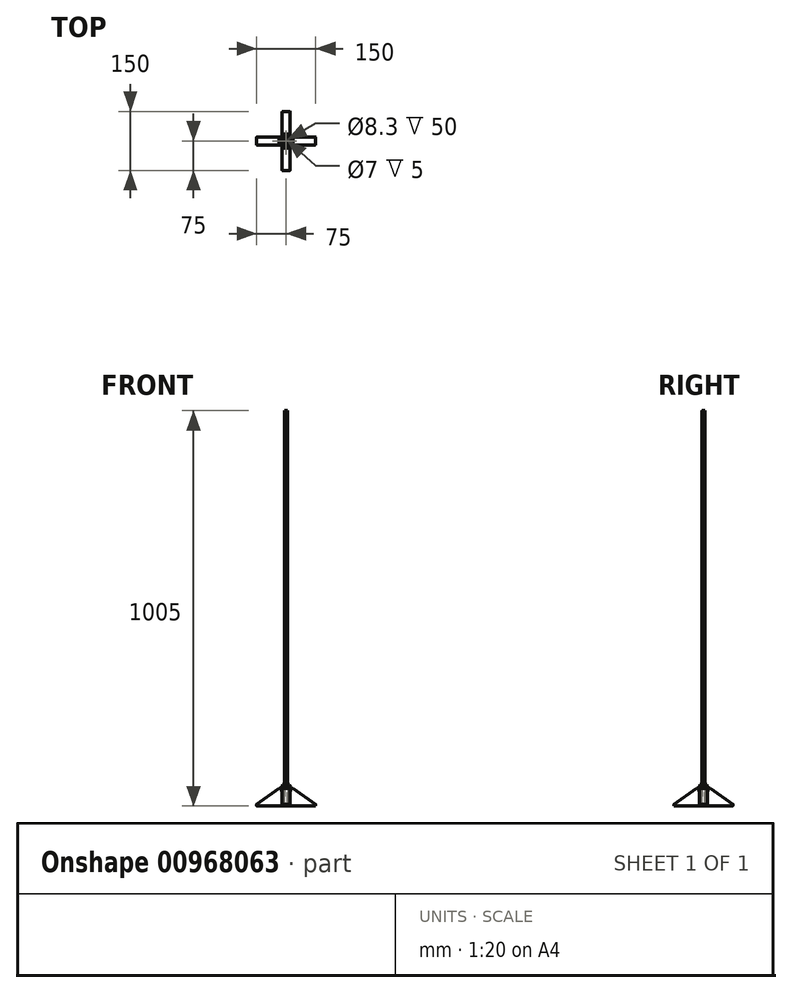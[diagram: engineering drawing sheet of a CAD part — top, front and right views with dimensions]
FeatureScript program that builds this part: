
annotation { "Feature Type Name" : "Feature", "Feature Type Description" : "" }
export const myFeature = defineFeature(function(context is Context, id is Id, definition is map)
    precondition{}
    {
        {
            var Q0;
            Q0=qCreatedBy(makeId("Top.planeOp"),FACE);
            var sketch = newSketch(context, id + "F0", { "sketchPlane" : qUnion([Q0])});
            skCircle(sketch, "E0", {"center": v(0, 0) * mm, "radius": 4.15 * mm});
            skCircle(sketch, "E1.0", {"center": v(0, 0) * mm, "radius": 9.15 * mm});
            skSolve(sketch);
        }
        {
            var Q0;
            Q0 = qSketchRegion(id + "F0", true);
            extrude(context, id + "F1", {"entities" : qUnion([Q0]), "depth" : 50 * mm, "offsetDistance" : 25 * mm});
        }
        {
            var Q0;
            Q0=makeQuery(id+"F1.opExtrude","CAP_FACE",FACE,{"disambiguationData":[OSD([sQuery(id+"F0.wireOp",EDGE,"E0"),sQuery(id+"F0.wireOp",EDGE,"E1.0")])],"isStart":true});
            var sketch = newSketch(context, id + "F2", { "sketchPlane" : qUnion([Q0])});
            skLineSegment(sketch, "E2.bottom", {"start": v(10, 75) * mm, "end": v(-10, 75) * mm});
            skLineSegment(sketch, "E2.top", {"start": v(10, -75) * mm, "end": v(-10, -75) * mm});
            skLineSegment(sketch, "E2.left", {"start": v(10, 75) * mm, "end": v(10, -75) * mm});
            skLineSegment(sketch, "E2.right", {"start": v(-10, 75) * mm, "end": v(-10, -75) * mm});
            skPoint(sketch, "E2.middle", {"position": v(0, 0) * mm});
            skLineSegment(sketch, "E3.bottom", {"start": v(75, 10) * mm, "end": v(-75, 10) * mm});
            skLineSegment(sketch, "E3.top", {"start": v(75, -10) * mm, "end": v(-75, -10) * mm});
            skLineSegment(sketch, "E3.left", {"start": v(75, 10) * mm, "end": v(75, -10) * mm});
            skLineSegment(sketch, "E3.right", {"start": v(-75, 10) * mm, "end": v(-75, -10) * mm});
            skSolve(sketch);
        }
        {
            var Q0;
            Q0 = qSketchRegion(id + "F2", true);
            extrude(context, id + "F3", {"entities" : qUnion([Q0]), "operationType" : NewBodyOperationType.ADD, "depth" : 5 * mm, "offsetDistance" : 25 * mm});
        }
        {
            var Q0;
            Q0=qCreatedBy(makeId("Right.planeOp"),FACE);
            var sketch = newSketch(context, id + "F4", { "sketchPlane" : qUnion([Q0])});
            skLineSegment(sketch, "E4", {"start": v(-75, 0) * mm, "end": v(0, 52.52) * mm});
            skLineSegment(sketch, "E5.MirrorCS", {"start": v(75, 0) * mm, "end": v(0, 52.52) * mm});
            skLineSegment(sketch, "E6", {"start": v(-75, 0) * mm, "end": v(-7, 0) * mm});
            skLineSegment(sketch, "E7", {"start": v(-7, 0) * mm, "end": v(-7, 47.61) * mm});
            skLineSegment(sketch, "E8.MirrorCS", {"start": v(7, 0) * mm, "end": v(7, 47.61) * mm});
            skLineSegment(sketch, "E9.MirrorCS", {"start": v(75, 0) * mm, "end": v(7, 0) * mm});
            skSolve(sketch);
        }
        {
            var Q0;
            {var subQ0=sQuery(id+"F4.wireOp",EDGE,"E6");Q0=makeQuery(id+"F4.imprint","IMPRINT",FACE,{"disambiguationData":[TD([[makeQuery(id+"F4.imprint","IMPRINT",EDGE,{"derivedFrom":subQ0}),1.0]])]});}
            var Q1;
            {var subQ2=sQuery(id+"F4.wireOp",EDGE,"E8.MirrorCS");Q1=makeQuery(id+"F4.imprint","IMPRINT",FACE,{"disambiguationData":[TD([[makeQuery(id+"F4.imprint","IMPRINT",EDGE,{"derivedFrom":subQ2}),-1.0]])]});}
            extrude(context, id + "F5", {"entities" : qUnion([Q0, Q1]), "operationType" : NewBodyOperationType.ADD, "endBound" : BoundingType.SYMMETRIC, "depth" : 20 * mm, "offsetDistance" : 25 * mm});
        }
        {
            var Q0;
            Q0=qCreatedBy(makeId("Front.planeOp"),FACE);
            var sketch = newSketch(context, id + "F6", { "sketchPlane" : qUnion([Q0])});
            skLineSegment(sketch, "E10", {"start": v(-75, 0) * mm, "end": v(0, 52.52) * mm});
            skLineSegment(sketch, "E11.MirrorCS", {"start": v(75, 0) * mm, "end": v(0, 52.52) * mm});
            skLineSegment(sketch, "E12", {"start": v(-75, 0) * mm, "end": v(-7, 0) * mm});
            skLineSegment(sketch, "E13", {"start": v(-7, 0) * mm, "end": v(-7, 47.61) * mm});
            skLineSegment(sketch, "E14.MirrorCS", {"start": v(7, 0) * mm, "end": v(7, 47.61) * mm});
            skLineSegment(sketch, "E15.MirrorCS", {"start": v(75, 0) * mm, "end": v(7, 0) * mm});
            skSolve(sketch);
        }
        {
            var Q0;
            Q0 = qSketchRegion(id + "F6", true);
            extrude(context, id + "F7", {"entities" : qUnion([Q0]), "operationType" : NewBodyOperationType.ADD, "endBound" : BoundingType.SYMMETRIC, "depth" : 20 * mm, "offsetDistance" : 25 * mm});
        }
        {
            var Q0;
            Q0=makeQuery(id+"F1.opExtrude","CAP_FACE",FACE,{"disambiguationData":[OSD([sQuery(id+"F0.wireOp",EDGE,"E0"),sQuery(id+"F0.wireOp",EDGE,"E1.0")])],"isStart":false});
            var sketch = newSketch(context, id + "F8", { "sketchPlane" : qUnion([Q0])});
            skCircle(sketch, "E16", {"center": v(0, 0) * mm, "radius": 9 * mm});
            skCircle(sketch, "E17", {"center": v(0, 0) * mm, "radius": 20 * mm});
            skSolve(sketch);
        }
        {
            var Q0;
            Q0 = qSketchRegion(id + "F8", true);
            extrude(context, id + "F9", {"entities" : qUnion([Q0]), "operationType" : NewBodyOperationType.REMOVE, "oppositeDirection" : true, "depth" : 10 * mm, "offsetDistance" : 25 * mm});
        }
        {
            var Q0;
            Q0=makeQuery(id+"F9.boolean.opBoolean","COPY",FACE,{"derivedFrom":makeQuery(id+"F9.opExtrude","CAP_FACE",FACE,{"disambiguationData":[OSD([sQuery(id+"F8.wireOp",EDGE,"E16"),sQuery(id+"F8.wireOp",EDGE,"E17")])],"isStart":false})});
            var sketch = newSketch(context, id + "F10", { "sketchPlane" : qUnion([Q0])});
            skCircle(sketch, "E18", {"center": v(0, 0) * mm, "radius": 12.5 * mm});
            skSolve(sketch);
        }
        {
            var Q0;
            {var subQ0=makeQuery(id+"F9.opExtrude","CAP_FACE",FACE,{"disambiguationData":[OSD([sQuery(id+"F8.wireOp",EDGE,"E16"),sQuery(id+"F8.wireOp",EDGE,"E17")])],"isStart":false});var subQ9=makeQuery(id+"F1.opExtrude","SWEPT_FACE",FACE,{"disambiguationData":[OSD([sQuery(id+"F0.wireOp",EDGE,"E1.0")])]});Q0=makeQuery(id+"F10.imprint","IMPRINT",FACE,{"disambiguationData":[TD([[makeQuery(id+"F10.imprint","IMPRINT",EDGE,{"derivedFrom":makeQuery(id+"F9.boolean.opBoolean","INTERSECT",EDGE,{"disambiguationData":[OD(0.0)],"derivedFrom":[subQ9,subQ0]})}),-1.0]])]});}
            var Q1;
            {var subQ0=makeQuery(id+"F9.opExtrude","CAP_FACE",FACE,{"disambiguationData":[OSD([sQuery(id+"F8.wireOp",EDGE,"E16"),sQuery(id+"F8.wireOp",EDGE,"E17")])],"isStart":false});var subQ9=makeQuery(id+"F1.opExtrude","SWEPT_FACE",FACE,{"disambiguationData":[OSD([sQuery(id+"F0.wireOp",EDGE,"E1.0")])]});Q1=makeQuery(id+"F10.imprint","IMPRINT",FACE,{"disambiguationData":[TD([[makeQuery(id+"F10.imprint","IMPRINT",EDGE,{"derivedFrom":makeQuery(id+"F9.boolean.opBoolean","INTERSECT",EDGE,{"disambiguationData":[OD(1.0)],"derivedFrom":[subQ9,subQ0]})}),-1.0]])]});}
            var Q2;
            {var subQ0=makeQuery(id+"F9.opExtrude","CAP_FACE",FACE,{"disambiguationData":[OSD([sQuery(id+"F8.wireOp",EDGE,"E16"),sQuery(id+"F8.wireOp",EDGE,"E17")])],"isStart":false});var subQ3=makeQuery(id+"F1.opExtrude","SWEPT_FACE",FACE,{"disambiguationData":[OSD([sQuery(id+"F0.wireOp",EDGE,"E1.0")])]});Q2=makeQuery(id+"F10.imprint","IMPRINT",FACE,{"disambiguationData":[TD([[makeQuery(id+"F10.imprint","IMPRINT",EDGE,{"derivedFrom":makeQuery(id+"F9.boolean.opBoolean","INTERSECT",EDGE,{"disambiguationData":[OD(2.0)],"derivedFrom":[subQ3,subQ0]})}),-1.0]])]});}
            var Q3;
            {var subQ0=makeQuery(id+"F9.opExtrude","CAP_FACE",FACE,{"disambiguationData":[OSD([sQuery(id+"F8.wireOp",EDGE,"E16"),sQuery(id+"F8.wireOp",EDGE,"E17")])],"isStart":false});var subQ3=makeQuery(id+"F1.opExtrude","SWEPT_FACE",FACE,{"disambiguationData":[OSD([sQuery(id+"F0.wireOp",EDGE,"E1.0")])]});Q3=makeQuery(id+"F10.imprint","IMPRINT",FACE,{"disambiguationData":[TD([[makeQuery(id+"F10.imprint","IMPRINT",EDGE,{"derivedFrom":makeQuery(id+"F9.boolean.opBoolean","INTERSECT",EDGE,{"disambiguationData":[OD(3.0)],"derivedFrom":[subQ3,subQ0]})}),-1.0]])]});}
            var Q4;
            Q4=makeQuery(id+"F10.imprint","IMPRINT",FACE,{"disambiguationData":[TD([[makeQuery(id+"F10.imprint","IMPRINT",EDGE,{"derivedFrom":sQuery(id+"F10.wireOp",EDGE,"E18")}),1.0]])]});
            extrude(context, id + "F11", {"entities" : qUnion([Q0, Q1, Q2, Q3, Q4]), "operationType" : NewBodyOperationType.ADD, "depth" : 5 * mm, "offsetDistance" : 25 * mm});
        }
        {
            var Q0;
            {var subQ2=sQuery(id+"F2.wireOp",EDGE,"E2.left");var subQ5=sQuery(id+"F2.wireOp",EDGE,"E2.bottom");var subQ6=makeQuery(id+"F3.opExtrude","SWEPT_FACE",FACE,{"disambiguationData":[OSD([subQ2]),TDD([makeQuery(id+"F2.imprint","IMPRINT",EDGE,{"disambiguationData":[TD([[makeQuery(id+"F2.imprint","INTERSECT",VERTEX,{"derivedFrom":[subQ5,subQ2]}),-1.0]])],"derivedFrom":subQ2})])]});var subQ7=sQuery(id+"F4.wireOp",EDGE,"E4");var subQ8=makeQuery(id+"F5.opExtrude","CAP_FACE",FACE,{"disambiguationData":[OSD([subQ7,sQuery(id+"F4.wireOp",EDGE,"E6"),sQuery(id+"F4.wireOp",EDGE,"E7")])],"isStart":false});Q0=makeQuery(id+"F7.boolean.opBoolean","SPLIT",FACE,{"disambiguationData":[TD([makeQuery(id+"F3.opExtrude","SWEPT_FACE",FACE,{"disambiguationData":[OSD([subQ5])]})])],"derivedFrom":makeQuery(id+"F5.boolean.opBoolean","MERGE",FACE,{"derivedFrom":[subQ6,subQ8]})});}
            var sketch = newSketch(context, id + "F12", { "sketchPlane" : qUnion([Q0])});
            skLineSegment(sketch, "E19.bottom", {"start": v(-13.66, 40) * mm, "end": v(-49.71, 40) * mm});
            skLineSegment(sketch, "E19.top", {"start": v(-13.66, 51.4) * mm, "end": v(-49.71, 51.4) * mm});
            skLineSegment(sketch, "E19.left", {"start": v(-13.66, 40) * mm, "end": v(-13.66, 51.4) * mm});
            skLineSegment(sketch, "E19.right", {"start": v(-49.71, 40) * mm, "end": v(-49.71, 51.4) * mm});
            skSolve(sketch);
        }
        {
            var Q0;
            Q0 = qSketchRegion(id + "F12", true);
            extrude(context, id + "F13", {"entities" : qUnion([Q0]), "operationType" : NewBodyOperationType.REMOVE, "oppositeDirection" : true, "depth" : 51.9 * mm, "offsetDistance" : 25 * mm});
        }
        {
            var Q0;
            {var subQ0=sQuery(id+"F2.wireOp",EDGE,"E3.bottom");Q0=makeQuery(id+"F7.boolean.opBoolean","MERGE",FACE,{"derivedFrom":[makeQuery(id+"F3.opExtrude","SWEPT_FACE",FACE,{"disambiguationData":[OSD([subQ0]),TDD([makeQuery(id+"F2.imprint","IMPRINT",EDGE,{"disambiguationData":[TD([[makeQuery(id+"F2.imprint","INTERSECT",VERTEX,{"derivedFrom":[subQ0,sQuery(id+"F2.wireOp",EDGE,"E3.right")]}),1.0]])],"derivedFrom":subQ0})])]}),makeQuery(id+"F7.opExtrude","CAP_FACE",FACE,{"disambiguationData":[OSD([sQuery(id+"F6.wireOp",EDGE,"E10"),sQuery(id+"F6.wireOp",EDGE,"E12"),sQuery(id+"F6.wireOp",EDGE,"E13")])],"isStart":false})]});}
            var sketch = newSketch(context, id + "F14", { "sketchPlane" : qUnion([Q0])});
            skLineSegment(sketch, "E20.bottom", {"start": v(-13.66, 40) * mm, "end": v(-64.64, 40) * mm});
            skLineSegment(sketch, "E20.top", {"start": v(-13.66, 50.99) * mm, "end": v(-64.64, 50.99) * mm});
            skLineSegment(sketch, "E20.left", {"start": v(-13.66, 40) * mm, "end": v(-13.66, 50.99) * mm});
            skLineSegment(sketch, "E20.right", {"start": v(-64.64, 40) * mm, "end": v(-64.64, 50.99) * mm});
            skSolve(sketch);
        }
        {
            var Q0;
            Q0 = qSketchRegion(id + "F14", true);
            extrude(context, id + "F15", {"entities" : qUnion([Q0]), "operationType" : NewBodyOperationType.REMOVE, "oppositeDirection" : true, "depth" : 25 * mm, "offsetDistance" : 25 * mm});
        }
        {
            var Q0;
            {var subQ2=sQuery(id+"F2.wireOp",EDGE,"E2.right");var subQ4=sQuery(id+"F2.wireOp",EDGE,"E2.top");var subQ6=makeQuery(id+"F3.opExtrude","SWEPT_FACE",FACE,{"disambiguationData":[OSD([subQ2]),TDD([makeQuery(id+"F2.imprint","IMPRINT",EDGE,{"disambiguationData":[TD([[makeQuery(id+"F2.imprint","INTERSECT",VERTEX,{"derivedFrom":[subQ4,subQ2]}),1.0]])],"derivedFrom":subQ2})])]});var subQ7=sQuery(id+"F4.wireOp",EDGE,"E5.MirrorCS");var subQ8=makeQuery(id+"F5.opExtrude","CAP_FACE",FACE,{"disambiguationData":[OSD([subQ7,sQuery(id+"F4.wireOp",EDGE,"E8.MirrorCS"),sQuery(id+"F4.wireOp",EDGE,"E9.MirrorCS")])],"isStart":true});Q0=makeQuery(id+"F7.boolean.opBoolean","SPLIT",FACE,{"disambiguationData":[TD([makeQuery(id+"F3.opExtrude","SWEPT_FACE",FACE,{"disambiguationData":[OSD([subQ4])]})])],"derivedFrom":makeQuery(id+"F5.boolean.opBoolean","MERGE",FACE,{"derivedFrom":[subQ6,subQ8]})});}
            var sketch = newSketch(context, id + "F16", { "sketchPlane" : qUnion([Q0])});
            skLineSegment(sketch, "E21.bottom", {"start": v(-15.31, 40) * mm, "end": v(-53.85, 40) * mm});
            skLineSegment(sketch, "E21.top", {"start": v(-15.31, 53.3) * mm, "end": v(-53.85, 53.3) * mm});
            skLineSegment(sketch, "E21.left", {"start": v(-15.31, 40) * mm, "end": v(-15.31, 53.3) * mm});
            skLineSegment(sketch, "E21.right", {"start": v(-53.85, 40) * mm, "end": v(-53.85, 53.3) * mm});
            skSolve(sketch);
        }
        {
            var Q0;
            Q0 = qSketchRegion(id + "F16", true);
            extrude(context, id + "F17", {"entities" : qUnion([Q0]), "operationType" : NewBodyOperationType.REMOVE, "oppositeDirection" : true, "depth" : 25 * mm, "offsetDistance" : 25 * mm});
        }
        {
            var Q0;
            {var subQ0=sQuery(id+"F2.wireOp",EDGE,"E3.top");Q0=makeQuery(id+"F7.boolean.opBoolean","MERGE",FACE,{"derivedFrom":[makeQuery(id+"F3.opExtrude","SWEPT_FACE",FACE,{"disambiguationData":[OSD([subQ0]),TDD([makeQuery(id+"F2.imprint","IMPRINT",EDGE,{"disambiguationData":[TD([[makeQuery(id+"F2.imprint","INTERSECT",VERTEX,{"derivedFrom":[subQ0,sQuery(id+"F2.wireOp",EDGE,"E3.left")]}),-1.0]])],"derivedFrom":subQ0})])]}),makeQuery(id+"F7.opExtrude","CAP_FACE",FACE,{"disambiguationData":[OSD([sQuery(id+"F6.wireOp",EDGE,"E11.MirrorCS"),sQuery(id+"F6.wireOp",EDGE,"E14.MirrorCS"),sQuery(id+"F6.wireOp",EDGE,"E15.MirrorCS")])],"isStart":true})]});}
            var sketch = newSketch(context, id + "F18", { "sketchPlane" : qUnion([Q0])});
            skLineSegment(sketch, "E22.bottom", {"start": v(-13.66, 40) * mm, "end": v(-70.3, 40) * mm});
            skLineSegment(sketch, "E22.top", {"start": v(-13.66, 49.17) * mm, "end": v(-70.3, 49.17) * mm});
            skLineSegment(sketch, "E22.left", {"start": v(-13.66, 40) * mm, "end": v(-13.66, 49.17) * mm});
            skLineSegment(sketch, "E22.right", {"start": v(-70.3, 40) * mm, "end": v(-70.3, 49.17) * mm});
            skSolve(sketch);
        }
        {
            var Q0;
            Q0 = qSketchRegion(id + "F18", true);
            extrude(context, id + "F19", {"entities" : qUnion([Q0]), "operationType" : NewBodyOperationType.REMOVE, "oppositeDirection" : true, "depth" : 25 * mm, "offsetDistance" : 25 * mm});
        }
        {
            var Q0;
            Q0=makeQuery(id+"F11.opExtrude","CAP_EDGE",EDGE,{"disambiguationData":[OSD([sQuery(id+"F10.wireOp",EDGE,"E18")])],"isStart":false});
            var Q1;
            Q1=makeQuery(id+"F9.boolean.opBoolean","COPY",EDGE,{"derivedFrom":makeQuery(id+"F9.opExtrude","CAP_EDGE",EDGE,{"disambiguationData":[OSD([sQuery(id+"F8.wireOp",EDGE,"E16")])],"isStart":true})});
            fillet(context, id + "F20", {"entities" : qUnion([Q0, Q1]), "radius" : 2 * mm, "tangentPropagation" : true, "allowEdgeOverflow" : false});
        }
        {
            var Q0;
            Q0=makeQuery(id+"F3.boolean.opBoolean","SPLIT",FACE,{"disambiguationData":[TD([makeQuery(id+"F1.opExtrude","SWEPT_FACE",FACE,{"disambiguationData":[OSD([sQuery(id+"F0.wireOp",EDGE,"E0")])]})])],"derivedFrom":makeQuery(id+"F3.opExtrude","CAP_FACE",FACE,{"disambiguationData":[OSD([sQuery(id+"F2.wireOp",EDGE,"E2.bottom"),sQuery(id+"F2.wireOp",EDGE,"E2.top"),sQuery(id+"F2.wireOp",EDGE,"E2.left"),sQuery(id+"F2.wireOp",EDGE,"E2.right"),sQuery(id+"F2.wireOp",EDGE,"E3.bottom"),sQuery(id+"F2.wireOp",EDGE,"E3.top"),sQuery(id+"F2.wireOp",EDGE,"E3.left"),sQuery(id+"F2.wireOp",EDGE,"E3.right")])],"isStart":true})});
            var sketch = newSketch(context, id + "F21", { "sketchPlane" : qUnion([Q0])});
            skCircle(sketch, "E23", {"center": v(0, 0) * mm, "radius": 3.5 * mm});
            skSolve(sketch);
        }
        {
            var Q0;
            Q0 = qSketchRegion(id + "F21", true);
            extrude(context, id + "F22", {"entities" : qUnion([Q0]), "operationType" : NewBodyOperationType.REMOVE, "oppositeDirection" : true, "depth" : 25 * mm, "offsetDistance" : 25 * mm});
        }
        {
            var Q0;
            {var subQ0=sQuery(id+"F2.wireOp",EDGE,"E3.bottom");var subQ1=sQuery(id+"F6.wireOp",EDGE,"E10");Q0=makeQuery(id+"F7.boolean.opBoolean","SPLIT",EDGE,{"disambiguationData":[topologyDisambiguationEdgeConnected([makeQuery(id+"F3.opExtrude","SWEPT_FACE",FACE,{"disambiguationData":[OSD([subQ0]),TDD([makeQuery(id+"F2.imprint","IMPRINT",EDGE,{"disambiguationData":[TD([[makeQuery(id+"F2.imprint","INTERSECT",VERTEX,{"derivedFrom":[subQ0,sQuery(id+"F2.wireOp",EDGE,"E3.right")]}),1.0]])],"derivedFrom":subQ0})])]}),makeQuery(id+"F7.opExtrude","SWEPT_FACE",FACE,{"disambiguationData":[OSD([subQ1])]}),makeQuery(id+"F7.opExtrude","CAP_FACE",FACE,{"disambiguationData":[OSD([subQ1,sQuery(id+"F6.wireOp",EDGE,"E12"),sQuery(id+"F6.wireOp",EDGE,"E13")])],"isStart":false})])],"derivedFrom":makeQuery(id+"F7.opExtrude","CAP_EDGE",EDGE,{"disambiguationData":[OSD([subQ1])],"isStart":false})});}
            var Q1;
            {var subQ3=sQuery(id+"F4.wireOp",EDGE,"E5.MirrorCS");var subQ4=sQuery(id+"F2.wireOp",EDGE,"E2.top");Q1=makeQuery(id+"F7.boolean.opBoolean","SPLIT",EDGE,{"disambiguationData":[TD([makeQuery(id+"F3.opExtrude","SWEPT_FACE",FACE,{"disambiguationData":[OSD([subQ4])]})])],"derivedFrom":makeQuery(id+"F5.opExtrude","CAP_EDGE",EDGE,{"disambiguationData":[OSD([subQ3])],"isStart":true})});}
            var Q2;
            {var subQ0=sQuery(id+"F2.wireOp",EDGE,"E3.top");var subQ1=sQuery(id+"F6.wireOp",EDGE,"E10");Q2=makeQuery(id+"F7.boolean.opBoolean","SPLIT",EDGE,{"disambiguationData":[topologyDisambiguationEdgeConnected([makeQuery(id+"F3.opExtrude","SWEPT_FACE",FACE,{"disambiguationData":[OSD([subQ0]),TDD([makeQuery(id+"F2.imprint","IMPRINT",EDGE,{"disambiguationData":[TD([[makeQuery(id+"F2.imprint","INTERSECT",VERTEX,{"derivedFrom":[subQ0,sQuery(id+"F2.wireOp",EDGE,"E3.right")]}),1.0]])],"derivedFrom":subQ0})])]}),makeQuery(id+"F7.opExtrude","SWEPT_FACE",FACE,{"disambiguationData":[OSD([subQ1])]}),makeQuery(id+"F7.opExtrude","CAP_FACE",FACE,{"disambiguationData":[OSD([subQ1,sQuery(id+"F6.wireOp",EDGE,"E12"),sQuery(id+"F6.wireOp",EDGE,"E13")])],"isStart":true})])],"derivedFrom":makeQuery(id+"F7.opExtrude","CAP_EDGE",EDGE,{"disambiguationData":[OSD([subQ1])],"isStart":true})});}
            var Q3;
            {var subQ0=sQuery(id+"F4.wireOp",EDGE,"E5.MirrorCS");var subQ4=sQuery(id+"F2.wireOp",EDGE,"E2.top");Q3=makeQuery(id+"F7.boolean.opBoolean","SPLIT",EDGE,{"disambiguationData":[TD([makeQuery(id+"F3.opExtrude","SWEPT_FACE",FACE,{"disambiguationData":[OSD([subQ4])]})])],"derivedFrom":makeQuery(id+"F5.opExtrude","CAP_EDGE",EDGE,{"disambiguationData":[OSD([subQ0])],"isStart":false})});}
            var Q4;
            {var subQ0=sQuery(id+"F2.wireOp",EDGE,"E3.top");var subQ1=sQuery(id+"F6.wireOp",EDGE,"E11.MirrorCS");Q4=makeQuery(id+"F7.boolean.opBoolean","SPLIT",EDGE,{"disambiguationData":[topologyDisambiguationEdgeConnected([makeQuery(id+"F3.opExtrude","SWEPT_FACE",FACE,{"disambiguationData":[OSD([subQ0]),TDD([makeQuery(id+"F2.imprint","IMPRINT",EDGE,{"disambiguationData":[TD([[makeQuery(id+"F2.imprint","INTERSECT",VERTEX,{"derivedFrom":[subQ0,sQuery(id+"F2.wireOp",EDGE,"E3.left")]}),-1.0]])],"derivedFrom":subQ0})])]}),makeQuery(id+"F7.opExtrude","SWEPT_FACE",FACE,{"disambiguationData":[OSD([subQ1])]}),makeQuery(id+"F7.opExtrude","CAP_FACE",FACE,{"disambiguationData":[OSD([subQ1,sQuery(id+"F6.wireOp",EDGE,"E14.MirrorCS"),sQuery(id+"F6.wireOp",EDGE,"E15.MirrorCS")])],"isStart":true})])],"derivedFrom":makeQuery(id+"F7.opExtrude","CAP_EDGE",EDGE,{"disambiguationData":[OSD([subQ1])],"isStart":true})});}
            var Q5;
            {var subQ0=sQuery(id+"F2.wireOp",EDGE,"E3.bottom");var subQ1=sQuery(id+"F6.wireOp",EDGE,"E11.MirrorCS");Q5=makeQuery(id+"F7.boolean.opBoolean","SPLIT",EDGE,{"disambiguationData":[topologyDisambiguationEdgeConnected([makeQuery(id+"F3.opExtrude","SWEPT_FACE",FACE,{"disambiguationData":[OSD([subQ0]),TDD([makeQuery(id+"F2.imprint","IMPRINT",EDGE,{"disambiguationData":[TD([[makeQuery(id+"F2.imprint","INTERSECT",VERTEX,{"derivedFrom":[subQ0,sQuery(id+"F2.wireOp",EDGE,"E3.left")]}),-1.0]])],"derivedFrom":subQ0})])]}),makeQuery(id+"F7.opExtrude","SWEPT_FACE",FACE,{"disambiguationData":[OSD([subQ1])]}),makeQuery(id+"F7.opExtrude","CAP_FACE",FACE,{"disambiguationData":[OSD([subQ1,sQuery(id+"F6.wireOp",EDGE,"E14.MirrorCS"),sQuery(id+"F6.wireOp",EDGE,"E15.MirrorCS")])],"isStart":false})])],"derivedFrom":makeQuery(id+"F7.opExtrude","CAP_EDGE",EDGE,{"disambiguationData":[OSD([subQ1])],"isStart":false})});}
            var Q6;
            {var subQ4=sQuery(id+"F4.wireOp",EDGE,"E4");var subQ5=sQuery(id+"F2.wireOp",EDGE,"E2.bottom");Q6=makeQuery(id+"F7.boolean.opBoolean","SPLIT",EDGE,{"disambiguationData":[TD([makeQuery(id+"F3.opExtrude","SWEPT_FACE",FACE,{"disambiguationData":[OSD([subQ5])]})])],"derivedFrom":makeQuery(id+"F5.opExtrude","CAP_EDGE",EDGE,{"disambiguationData":[OSD([subQ4])],"isStart":false})});}
            var Q7;
            {var subQ0=sQuery(id+"F4.wireOp",EDGE,"E4");var subQ5=sQuery(id+"F2.wireOp",EDGE,"E2.bottom");Q7=makeQuery(id+"F7.boolean.opBoolean","SPLIT",EDGE,{"disambiguationData":[TD([makeQuery(id+"F3.opExtrude","SWEPT_FACE",FACE,{"disambiguationData":[OSD([subQ5])]})])],"derivedFrom":makeQuery(id+"F5.opExtrude","CAP_EDGE",EDGE,{"disambiguationData":[OSD([subQ0])],"isStart":true})});}
            fillet(context, id + "F23", {"entities" : qUnion([Q0, Q1, Q2, Q3, Q4, Q5, Q6, Q7]), "radius" : 5 * mm, "tangentPropagation" : true, "allowEdgeOverflow" : false});
        }
        {
            var Q0;
            {var subQ0=sQuery(id+"F2.wireOp",EDGE,"E2.right");Q0=makeQuery(id+"F7.boolean.opBoolean","INTERSECT",EDGE,{"derivedFrom":[makeQuery(id+"F5.boolean.opBoolean","MERGE",FACE,{"derivedFrom":[makeQuery(id+"F3.opExtrude","SWEPT_FACE",FACE,{"disambiguationData":[OSD([subQ0]),TDD([makeQuery(id+"F2.imprint","IMPRINT",EDGE,{"disambiguationData":[TD([[makeQuery(id+"F2.imprint","INTERSECT",VERTEX,{"derivedFrom":[sQuery(id+"F2.wireOp",EDGE,"E2.bottom"),subQ0]}),-1.0]])],"derivedFrom":subQ0})])]}),makeQuery(id+"F5.opExtrude","CAP_FACE",FACE,{"disambiguationData":[OSD([sQuery(id+"F4.wireOp",EDGE,"E4"),sQuery(id+"F4.wireOp",EDGE,"E6"),sQuery(id+"F4.wireOp",EDGE,"E7")])],"isStart":true})]}),makeQuery(id+"F7.opExtrude","CAP_FACE",FACE,{"disambiguationData":[OSD([sQuery(id+"F6.wireOp",EDGE,"E10"),sQuery(id+"F6.wireOp",EDGE,"E12"),sQuery(id+"F6.wireOp",EDGE,"E13")])],"isStart":false})]});}
            var Q1;
            {var subQ0=sQuery(id+"F2.wireOp",EDGE,"E2.left");Q1=makeQuery(id+"F7.boolean.opBoolean","INTERSECT",EDGE,{"derivedFrom":[makeQuery(id+"F5.boolean.opBoolean","MERGE",FACE,{"derivedFrom":[makeQuery(id+"F3.opExtrude","SWEPT_FACE",FACE,{"disambiguationData":[OSD([subQ0]),TDD([makeQuery(id+"F2.imprint","IMPRINT",EDGE,{"disambiguationData":[TD([[makeQuery(id+"F2.imprint","INTERSECT",VERTEX,{"derivedFrom":[sQuery(id+"F2.wireOp",EDGE,"E2.bottom"),subQ0]}),-1.0]])],"derivedFrom":subQ0})])]}),makeQuery(id+"F5.opExtrude","CAP_FACE",FACE,{"disambiguationData":[OSD([sQuery(id+"F4.wireOp",EDGE,"E4"),sQuery(id+"F4.wireOp",EDGE,"E6"),sQuery(id+"F4.wireOp",EDGE,"E7")])],"isStart":false})]}),makeQuery(id+"F7.opExtrude","CAP_FACE",FACE,{"disambiguationData":[OSD([sQuery(id+"F6.wireOp",EDGE,"E11.MirrorCS"),sQuery(id+"F6.wireOp",EDGE,"E14.MirrorCS"),sQuery(id+"F6.wireOp",EDGE,"E15.MirrorCS")])],"isStart":false})]});}
            var Q2;
            {var subQ0=sQuery(id+"F2.wireOp",EDGE,"E2.left");Q2=makeQuery(id+"F7.boolean.opBoolean","INTERSECT",EDGE,{"derivedFrom":[makeQuery(id+"F5.boolean.opBoolean","MERGE",FACE,{"derivedFrom":[makeQuery(id+"F3.opExtrude","SWEPT_FACE",FACE,{"disambiguationData":[OSD([subQ0]),TDD([makeQuery(id+"F2.imprint","IMPRINT",EDGE,{"disambiguationData":[TD([[makeQuery(id+"F2.imprint","INTERSECT",VERTEX,{"derivedFrom":[sQuery(id+"F2.wireOp",EDGE,"E2.top"),subQ0]}),1.0]])],"derivedFrom":subQ0})])]}),makeQuery(id+"F5.opExtrude","CAP_FACE",FACE,{"disambiguationData":[OSD([sQuery(id+"F4.wireOp",EDGE,"E5.MirrorCS"),sQuery(id+"F4.wireOp",EDGE,"E8.MirrorCS"),sQuery(id+"F4.wireOp",EDGE,"E9.MirrorCS")])],"isStart":false})]}),makeQuery(id+"F7.opExtrude","CAP_FACE",FACE,{"disambiguationData":[OSD([sQuery(id+"F6.wireOp",EDGE,"E11.MirrorCS"),sQuery(id+"F6.wireOp",EDGE,"E14.MirrorCS"),sQuery(id+"F6.wireOp",EDGE,"E15.MirrorCS")])],"isStart":true})]});}
            var Q3;
            {var subQ0=sQuery(id+"F2.wireOp",EDGE,"E2.right");Q3=makeQuery(id+"F7.boolean.opBoolean","INTERSECT",EDGE,{"derivedFrom":[makeQuery(id+"F5.boolean.opBoolean","MERGE",FACE,{"derivedFrom":[makeQuery(id+"F3.opExtrude","SWEPT_FACE",FACE,{"disambiguationData":[OSD([subQ0]),TDD([makeQuery(id+"F2.imprint","IMPRINT",EDGE,{"disambiguationData":[TD([[makeQuery(id+"F2.imprint","INTERSECT",VERTEX,{"derivedFrom":[sQuery(id+"F2.wireOp",EDGE,"E2.top"),subQ0]}),1.0]])],"derivedFrom":subQ0})])]}),makeQuery(id+"F5.opExtrude","CAP_FACE",FACE,{"disambiguationData":[OSD([sQuery(id+"F4.wireOp",EDGE,"E5.MirrorCS"),sQuery(id+"F4.wireOp",EDGE,"E8.MirrorCS"),sQuery(id+"F4.wireOp",EDGE,"E9.MirrorCS")])],"isStart":true})]}),makeQuery(id+"F7.opExtrude","CAP_FACE",FACE,{"disambiguationData":[OSD([sQuery(id+"F6.wireOp",EDGE,"E10"),sQuery(id+"F6.wireOp",EDGE,"E12"),sQuery(id+"F6.wireOp",EDGE,"E13")])],"isStart":true})]});}
            fillet(context, id + "F24", {"entities" : qUnion([Q0, Q1, Q2, Q3]), "radius" : 5 * mm, "tangentPropagation" : true, "allowEdgeOverflow" : false});
        }
        {
            var Q0;
            Q0=makeQuery(id+"F1.opExtrude","CAP_FACE",FACE,{"disambiguationData":[OSD([sQuery(id+"F0.wireOp",EDGE,"E0"),sQuery(id+"F0.wireOp",EDGE,"E1.0")])],"isStart":false});
            var sketch = newSketch(context, id + "F25", { "sketchPlane" : qUnion([Q0])});
            skCircle(sketch, "E24", {"center": v(0, 0) * mm, "radius": 4 * mm});
            skSolve(sketch);
        }
        {
            var Q0;
            Q0 = qSketchRegion(id + "F25", true);
            extrude(context, id + "F26", {"entities" : qUnion([Q0]), "oppositeDirection" : true, "depth" : 50 * mm, "offsetDistance" : 25 * mm});
        }
        {
            var Q0;
            Q0=makeQuery(id+"F26.opExtrude","CAP_FACE",FACE,{"disambiguationData":[OSD([sQuery(id+"F25.wireOp",EDGE,"E24")])],"isStart":true});
            extrude(context, id + "F27", {"entities" : qUnion([Q0]), "operationType" : NewBodyOperationType.ADD, "depth" : 950 * mm, "offsetDistance" : 25 * mm});
        }
    });
